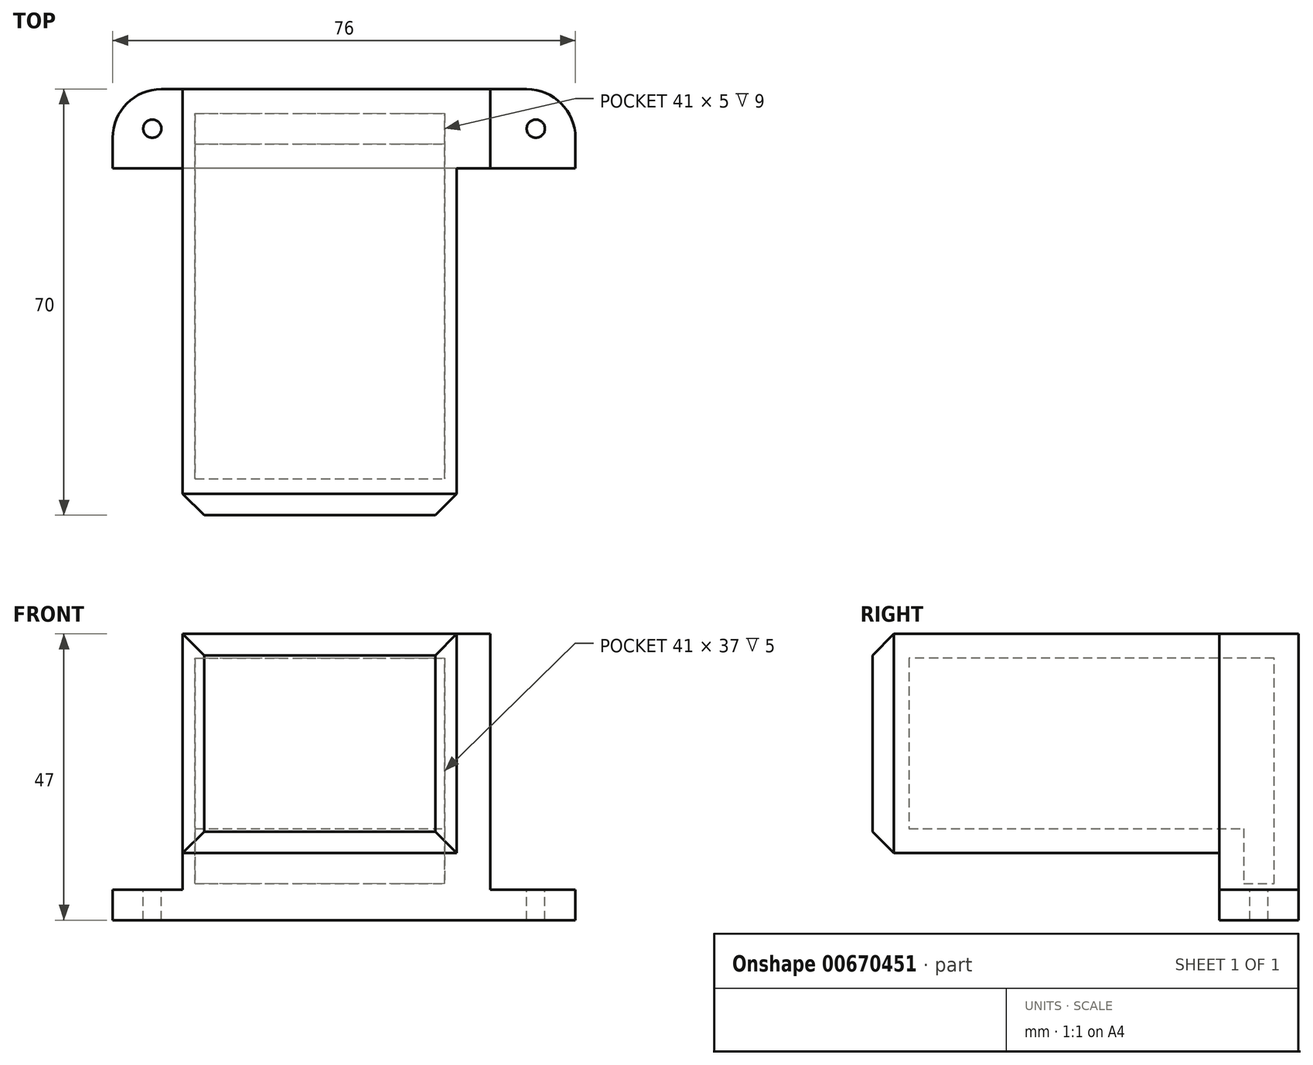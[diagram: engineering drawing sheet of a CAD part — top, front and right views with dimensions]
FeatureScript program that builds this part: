
annotation { "Feature Type Name" : "Feature", "Feature Type Description" : "" }
export const myFeature = defineFeature(function(context is Context, id is Id, definition is map)
    precondition{}
    {
        {
            var Q0;
            Q0=qCreatedBy(makeId("Top.planeOp"),FACE);
            var sketch = newSketch(context, id + "F0", { "sketchPlane" : qUnion([Q0])});
            skLineSegment(sketch, "E0.bottom", {"start": v(38, -6.5) * mm, "end": v(-38, -6.5) * mm});
            skLineSegment(sketch, "E0.top", {"start": v(38, 6.5) * mm, "end": v(-38, 6.5) * mm});
            skLineSegment(sketch, "E0.left", {"start": v(38, -6.5) * mm, "end": v(38, 6.5) * mm});
            skLineSegment(sketch, "E0.right", {"start": v(-38, -6.5) * mm, "end": v(-38, 6.5) * mm});
            skPoint(sketch, "E0.middle", {"position": v(0, 0) * mm});
            skSolve(sketch);
        }
        {
            var Q0;
            Q0 = qSketchRegion(id + "F0", true);
            extrude(context, id + "F1", {"entities" : qUnion([Q0]), "depth" : 2 * mm, "offsetDistance" : 25 * mm});
        }
        {
            var Q0;
            Q0=makeQuery(id+"F1.opExtrude","SWEPT_EDGE",EDGE,{"disambiguationData":[OSD([sQuery(id+"F0.wireOp",EDGE,"E0.top"),sQuery(id+"F0.wireOp",EDGE,"E0.right")])]});
            var Q1;
            Q1=makeQuery(id+"F1.opExtrude","SWEPT_EDGE",EDGE,{"disambiguationData":[OSD([sQuery(id+"F0.wireOp",EDGE,"E0.top"),sQuery(id+"F0.wireOp",EDGE,"E0.left")])]});
            fillet(context, id + "F2", {"entities" : qUnion([Q0, Q1]), "radius" : 8 * mm, "tangentPropagation" : true, "allowEdgeOverflow" : false});
        }
        {
            var Q0;
            Q0=makeQuery(id+"F1.opExtrude","CAP_FACE",FACE,{"disambiguationData":[OSD([sQuery(id+"F0.wireOp",EDGE,"E0.bottom"),sQuery(id+"F0.wireOp",EDGE,"E0.top"),sQuery(id+"F0.wireOp",EDGE,"E0.left"),sQuery(id+"F0.wireOp",EDGE,"E0.right")])],"isStart":false});
            var sketch = newSketch(context, id + "F3", { "sketchPlane" : qUnion([Q0])});
            skLineSegment(sketch, "E1.bottom", {"start": v(16.5, 6.5) * mm, "end": v(-26.5, 6.5) * mm});
            skLineSegment(sketch, "E1.top", {"start": v(16.5, -6.5) * mm, "end": v(-26.5, -6.5) * mm});
            skLineSegment(sketch, "E1.left", {"start": v(16.5, 6.5) * mm, "end": v(16.5, -6.5) * mm});
            skLineSegment(sketch, "E1.right", {"start": v(-26.5, 6.5) * mm, "end": v(-26.5, -6.5) * mm});
            skSolve(sketch);
        }
        {
            var Q0;
            Q0 = qSketchRegion(id + "F3", true);
            extrude(context, id + "F4", {"entities" : qUnion([Q0]), "operationType" : NewBodyOperationType.ADD, "depth" : 9 * mm, "offsetDistance" : 25 * mm});
        }
        {
            var Q0;
            Q0=makeQuery(id+"F4.boolean.opBoolean","MERGE",FACE,{"derivedFrom":[makeQuery(id+"F1.opExtrude","SWEPT_FACE",FACE,{"disambiguationData":[OSD([sQuery(id+"F0.wireOp",EDGE,"E0.top")])]}),makeQuery(id+"F4.opExtrude","SWEPT_FACE",FACE,{"disambiguationData":[OSD([sQuery(id+"F3.wireOp",EDGE,"E1.bottom")])]})]});
            var sketch = newSketch(context, id + "F5", { "sketchPlane" : qUnion([Q0])});
            skLineSegment(sketch, "E2.bottom", {"start": v(-16.5, 11) * mm, "end": v(26.5, 11) * mm});
            skLineSegment(sketch, "E2.top", {"start": v(-16.5, 47) * mm, "end": v(26.5, 47) * mm});
            skLineSegment(sketch, "E2.left", {"start": v(-16.5, 11) * mm, "end": v(-16.5, 47) * mm});
            skLineSegment(sketch, "E2.right", {"start": v(26.5, 11) * mm, "end": v(26.5, 47) * mm});
            skSolve(sketch);
        }
        {
            var Q0;
            Q0 = qSketchRegion(id + "F5", true);
            extrude(context, id + "F6", {"entities" : qUnion([Q0]), "operationType" : NewBodyOperationType.ADD, "oppositeDirection" : true, "depth" : 70 * mm, "offsetDistance" : 25 * mm});
        }
        {
            var Q0;
            Q0=makeQuery(id+"F6.boolean.opBoolean","MERGE",FACE,{"derivedFrom":[makeQuery(id+"F4.opExtrude","SWEPT_FACE",FACE,{"disambiguationData":[OSD([sQuery(id+"F3.wireOp",EDGE,"E1.left")])]}),makeQuery(id+"F6.opExtrude","SWEPT_FACE",FACE,{"disambiguationData":[OSD([sQuery(id+"F5.wireOp",EDGE,"E2.left")])]})]});
            var sketch = newSketch(context, id + "F7", { "sketchPlane" : qUnion([Q0])});
            skLineSegment(sketch, "E3.0", {"start": v(-2.5, 15) * mm, "end": v(-2.5, 6) * mm});
            skLineSegment(sketch, "E3.1", {"start": v(2.5, 6) * mm, "end": v(2.5, 43) * mm});
            skLineSegment(sketch, "E3.2", {"start": v(2.5, 43) * mm, "end": v(-57.5, 43) * mm});
            skLineSegment(sketch, "E3.3", {"start": v(-2.5, 6) * mm, "end": v(2.5, 6) * mm});
            skLineSegment(sketch, "E3.5", {"start": v(-57.5, 15) * mm, "end": v(-2.5, 15) * mm});
            skLineSegment(sketch, "E4", {"start": v(-57.5, 43) * mm, "end": v(-57.5, 15) * mm});
            skSolve(sketch);
        }
        {
            var Q0;
            Q0 = qSketchRegion(id + "F7", true);
            extrude(context, id + "F8", {"entities" : qUnion([Q0]), "operationType" : NewBodyOperationType.REMOVE, "oppositeDirection" : true, "depth" : 41 * mm, "offsetDistance" : 25 * mm});
        }
        {
            var Q0;
            Q0=makeQuery(id+"F6.boolean.opBoolean","MERGE",FACE,{"derivedFrom":[makeQuery(id+"F4.opExtrude","SWEPT_FACE",FACE,{"disambiguationData":[OSD([sQuery(id+"F3.wireOp",EDGE,"E1.left")])]}),makeQuery(id+"F6.opExtrude","SWEPT_FACE",FACE,{"disambiguationData":[OSD([sQuery(id+"F5.wireOp",EDGE,"E2.left")])]})]});
            var sketch = newSketch(context, id + "F9", { "sketchPlane" : qUnion([Q0])});
            skLineSegment(sketch, "E5.0", {"start": v(-6.5, 11) * mm, "end": v(-6.5, 2) * mm});
            skLineSegment(sketch, "E6.0", {"start": v(-63.5, 11) * mm, "end": v(-6.5, 11) * mm});
            skLineSegment(sketch, "E7.0", {"start": v(-63.5, 11) * mm, "end": v(-63.5, 47) * mm});
            skLineSegment(sketch, "E8.0", {"start": v(-63.5, 47) * mm, "end": v(6.5, 47) * mm});
            skLineSegment(sketch, "E9.0", {"start": v(6.5, 47) * mm, "end": v(6.5, 2) * mm});
            skLineSegment(sketch, "E10.0", {"start": v(6.5, 2) * mm, "end": v(-6.5, 2) * mm});
            skSolve(sketch);
        }
        {
            var Q0;
            Q0 = qSketchRegion(id + "F9", true);
            extrude(context, id + "F10", {"entities" : qUnion([Q0]), "operationType" : NewBodyOperationType.ADD, "depth" : 2 * mm, "offsetDistance" : 25 * mm});
        }
        {
            var Q0;
            {var subQ0=sQuery(id+"F0.wireOp",EDGE,"E0.left");var subQ1=sQuery(id+"F0.wireOp",EDGE,"E0.top");var subQ2=sQuery(id+"F0.wireOp",EDGE,"E0.bottom");Q0=makeQuery(id+"F4.boolean.opBoolean","SPLIT",FACE,{"disambiguationData":[TD([makeQuery(id+"F1.opExtrude","SWEPT_FACE",FACE,{"disambiguationData":[OSD([subQ0])]})])],"derivedFrom":makeQuery(id+"F1.opExtrude","CAP_FACE",FACE,{"disambiguationData":[OSD([subQ2,subQ1,subQ0,sQuery(id+"F0.wireOp",EDGE,"E0.right")])],"isStart":false})});}
            var sketch = newSketch(context, id + "F11", { "sketchPlane" : qUnion([Q0])});
            skLineSegment(sketch, "E11.0.0", {"start": v(-26.5, -6.5) * mm, "end": v(-26.5, 6.5) * mm});
            skLineSegment(sketch, "E11.0.1", {"start": v(-26.5, 6.5) * mm, "end": v(-30, 6.5) * mm});
            skArc(sketch, "E11.0.2", {"start": v(-30, 6.5) * mm, "mid": v(-35.66, 4.16) * mm, "end": v(-38, -1.5) * mm});
            skLineSegment(sketch, "E11.0.3", {"start": v(-38, -1.5) * mm, "end": v(-38, -6.5) * mm});
            skLineSegment(sketch, "E11.0.4", {"start": v(-38, -6.5) * mm, "end": v(-26.5, -6.5) * mm});
            skLineSegment(sketch, "E12.0.0", {"start": v(30, 6.5) * mm, "end": v(18.5, 6.5) * mm});
            skLineSegment(sketch, "E12.0.1", {"start": v(18.5, 6.5) * mm, "end": v(18.5, -6.5) * mm});
            skLineSegment(sketch, "E12.0.2", {"start": v(18.5, -6.5) * mm, "end": v(38, -6.5) * mm});
            skLineSegment(sketch, "E12.0.3", {"start": v(38, -6.5) * mm, "end": v(38, -1.5) * mm});
            skArc(sketch, "E12.0.4", {"start": v(38, -1.5) * mm, "mid": v(35.66, 4.16) * mm, "end": v(30, 6.5) * mm});
            skSolve(sketch);
        }
        {
            var Q0;
            Q0 = qSketchRegion(id + "F11", true);
            extrude(context, id + "F12", {"entities" : qUnion([Q0]), "operationType" : NewBodyOperationType.ADD, "depth" : 3 * mm, "offsetDistance" : 25 * mm});
        }
        {
            var Q0;
            Q0=makeQuery(id+"F12.opExtrude","CAP_FACE",FACE,{"disambiguationData":[OSD([sQuery(id+"F11.wireOp",EDGE,"E11.0.0"),sQuery(id+"F11.wireOp",EDGE,"E11.0.1"),sQuery(id+"F11.wireOp",EDGE,"E11.0.2"),sQuery(id+"F11.wireOp",EDGE,"E11.0.3"),sQuery(id+"F11.wireOp",EDGE,"E11.0.4")])],"isStart":false});
            var sketch = newSketch(context, id + "F13", { "sketchPlane" : qUnion([Q0])});
            skCircle(sketch, "E13", {"center": v(-31.5, 0) * mm, "radius": 1.5 * mm});
            skCircle(sketch, "E14", {"center": v(31.5, 0) * mm, "radius": 1.5 * mm});
            skPoint(sketch, "E15.0.end.orphan", {"position": v(18.5, -6.5) * mm});
            skSolve(sketch);
        }
        {
            var Q0;
            Q0 = qSketchRegion(id + "F13", true);
            extrude(context, id + "F14", {"entities" : qUnion([Q0]), "operationType" : NewBodyOperationType.REMOVE, "oppositeDirection" : true, "depth" : 25 * mm, "offsetDistance" : 25 * mm});
        }
        {
            var Q0;
            Q0=makeQuery(id+"F12.opExtrude","CAP_FACE",FACE,{"disambiguationData":[OSD([sQuery(id+"F11.wireOp",EDGE,"E12.0.0"),sQuery(id+"F11.wireOp",EDGE,"E12.0.1"),sQuery(id+"F11.wireOp",EDGE,"E12.0.2"),sQuery(id+"F11.wireOp",EDGE,"E12.0.3"),sQuery(id+"F11.wireOp",EDGE,"E12.0.4")])],"isStart":false});
            var sketch = newSketch(context, id + "F15", { "sketchPlane" : qUnion([Q0])});
            skLineSegment(sketch, "E16.bottom", {"start": v(18.5, -6.5) * mm, "end": v(24, -6.5) * mm});
            skLineSegment(sketch, "E16.top", {"start": v(18.5, 6.5) * mm, "end": v(24, 6.5) * mm});
            skLineSegment(sketch, "E16.left", {"start": v(18.5, -6.5) * mm, "end": v(18.5, 6.5) * mm});
            skLineSegment(sketch, "E16.right", {"start": v(24, -6.5) * mm, "end": v(24, 6.5) * mm});
            skSolve(sketch);
        }
        {
            var Q0;
            Q0 = qSketchRegion(id + "F15", true);
            extrude(context, id + "F16", {"entities" : qUnion([Q0]), "operationType" : NewBodyOperationType.ADD, "depth" : 42 * mm, "offsetDistance" : 25 * mm});
        }
        {
            var Q0;
            Q0=makeQuery(id+"F10.opExtrude","CAP_EDGE",EDGE,{"disambiguationData":[OSD([sQuery(id+"F9.wireOp",EDGE,"E7.0")])],"isStart":false});
            var Q1;
            Q1=makeQuery(id+"F10.boolean.opBoolean","MERGE",EDGE,{"derivedFrom":[makeQuery(id+"F6.opExtrude","CAP_EDGE",EDGE,{"disambiguationData":[OSD([sQuery(id+"F5.wireOp",EDGE,"E2.top")])],"isStart":false}),makeQuery(id+"F10.opExtrude","SWEPT_EDGE",EDGE,{"disambiguationData":[OSD([sQuery(id+"F9.wireOp",EDGE,"E7.0"),sQuery(id+"F9.wireOp",EDGE,"E8.0")])]})]});
            var Q2;
            Q2=makeQuery(id+"F10.boolean.opBoolean","MERGE",EDGE,{"derivedFrom":[makeQuery(id+"F6.opExtrude","CAP_EDGE",EDGE,{"disambiguationData":[OSD([sQuery(id+"F5.wireOp",EDGE,"E2.bottom")])],"isStart":false}),makeQuery(id+"F10.opExtrude","SWEPT_EDGE",EDGE,{"disambiguationData":[OSD([sQuery(id+"F9.wireOp",EDGE,"E6.0"),sQuery(id+"F9.wireOp",EDGE,"E7.0")])]})]});
            var Q3;
            Q3=makeQuery(id+"F6.opExtrude","CAP_EDGE",EDGE,{"disambiguationData":[OSD([sQuery(id+"F5.wireOp",EDGE,"E2.right")])],"isStart":false});
            chamfer(context, id + "F17", {"entities" : qUnion([Q0, Q1, Q2, Q3]), "width" : 3.5 * mm, "tangentPropagation" : true});
        }
    });
